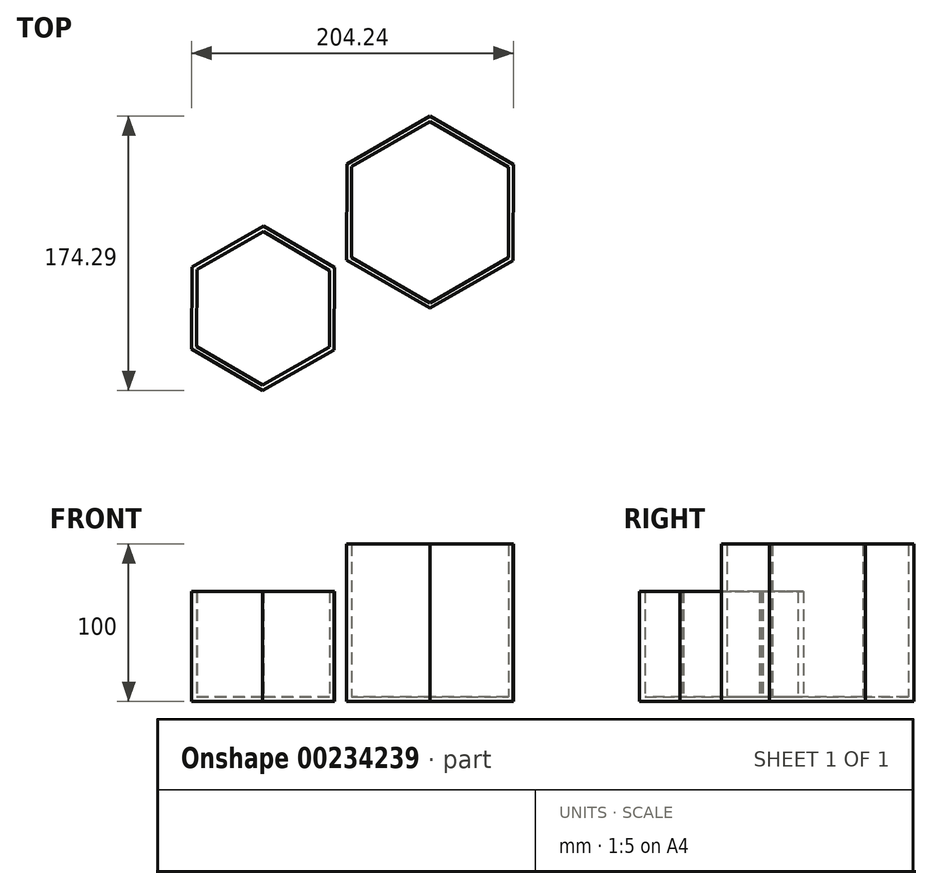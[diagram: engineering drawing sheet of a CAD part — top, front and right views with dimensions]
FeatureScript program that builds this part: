
annotation { "Feature Type Name" : "Feature", "Feature Type Description" : "" }
export const myFeature = defineFeature(function(context is Context, id is Id, definition is map)
    precondition{}
    {
        {
            var Q0;
            Q0=qCreatedBy(makeId("Top.planeOp"),FACE);
            var sketch = newSketch(context, id + "F0", { "sketchPlane" : qUnion([Q0])});
            skCircle(sketch, "E0.cCircle", {"center": v(0, 0) * mm, "radius": 52.86 * mm, "construction": true});
            skLineSegment(sketch, "E0.0", {"start": v(52.79, -30.64) * mm, "end": v(-0.14, -61.03) * mm});
            skLineSegment(sketch, "E0.1", {"start": v(-0.14, -61.03) * mm, "end": v(-52.93, -30.4) * mm});
            skLineSegment(sketch, "E0.2", {"start": v(-52.93, -30.4) * mm, "end": v(-52.79, 30.64) * mm});
            skLineSegment(sketch, "E0.3", {"start": v(-52.79, 30.64) * mm, "end": v(0.14, 61.03) * mm});
            skLineSegment(sketch, "E0.4", {"start": v(0.14, 61.03) * mm, "end": v(52.93, 30.4) * mm});
            skLineSegment(sketch, "E0.5", {"start": v(52.93, 30.4) * mm, "end": v(52.79, -30.64) * mm});
            skPoint(sketch, "E0.0.midPoint", {"position": v(26.32, -45.84) * mm});
            skCircle(sketch, "E1.cCircle", {"center": v(-105.99, -61.08) * mm, "radius": 45.2 * mm, "construction": true});
            skLineSegment(sketch, "E1.0", {"start": v(-60.93, -87.4) * mm, "end": v(-106.25, -113.26) * mm});
            skLineSegment(sketch, "E1.1", {"start": v(-106.25, -113.26) * mm, "end": v(-151.31, -86.94) * mm});
            skLineSegment(sketch, "E1.2", {"start": v(-151.31, -86.94) * mm, "end": v(-151.05, -34.75) * mm});
            skLineSegment(sketch, "E1.3", {"start": v(-151.05, -34.75) * mm, "end": v(-105.72, -8.89) * mm});
            skLineSegment(sketch, "E1.4", {"start": v(-105.72, -8.89) * mm, "end": v(-60.66, -35.21) * mm});
            skLineSegment(sketch, "E1.5", {"start": v(-60.66, -35.21) * mm, "end": v(-60.93, -87.4) * mm});
            skPoint(sketch, "E1.0.midPoint", {"position": v(-83.59, -100.33) * mm});
            skSolve(sketch);
        }
        {
            var Q0;
            Q0=makeQuery(id+"F0.imprint","IMPRINT",FACE,{"disambiguationData":[TD([[makeQuery(id+"F0.imprint","IMPRINT",EDGE,{"derivedFrom":sQuery(id+"F0.wireOp",EDGE,"E0.0")}),-1.0]])]});
            extrude(context, id + "F1", {"entities" : qUnion([Q0]), "depth" : 100 * mm});
        }
        {
            var Q0;
            Q0=makeQuery(id+"F0.imprint","IMPRINT",FACE,{"disambiguationData":[TD([[makeQuery(id+"F0.imprint","IMPRINT",EDGE,{"derivedFrom":sQuery(id+"F0.wireOp",EDGE,"E1.0")}),-1.0]])]});
            extrude(context, id + "F2", {"entities" : qUnion([Q0]), "depth" : 70 * mm});
        }
        {
            var Q0;
            Q0=makeQuery(id+"F2.opExtrude","CAP_FACE",FACE,{"disambiguationData":[OSD([sQuery(id+"F0.wireOp",EDGE,"E1.0"),sQuery(id+"F0.wireOp",EDGE,"E1.1"),sQuery(id+"F0.wireOp",EDGE,"E1.2"),sQuery(id+"F0.wireOp",EDGE,"E1.3"),sQuery(id+"F0.wireOp",EDGE,"E1.4"),sQuery(id+"F0.wireOp",EDGE,"E1.5")])],"isStart":false});
            shell(context, id + "F3", {"entities" : qUnion([Q0]), "thickness" : 3 * mm});
        }
        {
            var Q0;
            Q0=makeQuery(id+"F1.opExtrude","CAP_FACE",FACE,{"disambiguationData":[OSD([sQuery(id+"F0.wireOp",EDGE,"E0.0"),sQuery(id+"F0.wireOp",EDGE,"E0.1"),sQuery(id+"F0.wireOp",EDGE,"E0.2"),sQuery(id+"F0.wireOp",EDGE,"E0.3"),sQuery(id+"F0.wireOp",EDGE,"E0.4"),sQuery(id+"F0.wireOp",EDGE,"E0.5")])],"isStart":false});
            shell(context, id + "F4", {"entities" : qUnion([Q0]), "thickness" : 3 * mm});
        }
    });
